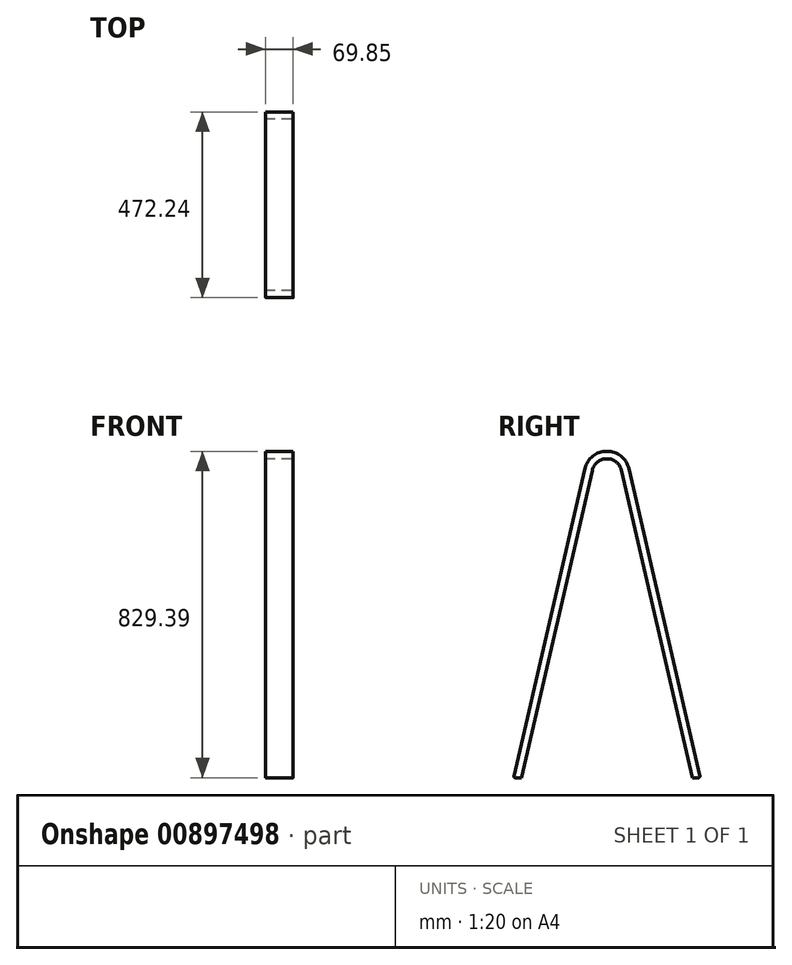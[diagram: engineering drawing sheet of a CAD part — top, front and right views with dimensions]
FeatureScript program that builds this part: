
annotation { "Feature Type Name" : "Feature", "Feature Type Description" : "" }
export const myFeature = defineFeature(function(context is Context, id is Id, definition is map)
    precondition{}
    {
        {
            var Q0;
            Q0=qCreatedBy(makeId("Right.planeOp"),FACE);
            var sketch = newSketch(context, id + "F0", { "sketchPlane" : qUnion([Q0])});
            skLineSegment(sketch, "E0", {"start": v(-210.57, 0) * mm, "end": v(-191.02, 0) * mm});
            skArc(sketch, "E1", {"start": v(63.5, 780.8) * mm, "mid": v(26.37, 810.34) * mm, "end": v(-10.75, 780.8) * mm});
            skLineSegment(sketch, "E2", {"start": v(63.5, 780.8) * mm, "end": v(243.76, 0) * mm});
            skLineSegment(sketch, "E3", {"start": v(-10.75, 780.8) * mm, "end": v(-191.02, 0) * mm});
            skLineSegment(sketch, "E4.0", {"start": v(-29.31, 785.1) * mm, "end": v(-210.57, 0) * mm});
            skLineSegment(sketch, "E4.2", {"start": v(82.06, 785.1) * mm, "end": v(263.3, 0) * mm});
            skArc(sketch, "E5.0", {"start": v(82.06, 785.1) * mm, "mid": v(26.37, 829.39) * mm, "end": v(-29.31, 785.1) * mm});
            skLineSegment(sketch, "E6.trimOffspring", {"start": v(243.76, 0) * mm, "end": v(263.3, 0) * mm});
            skPoint(sketch, "E7.start.orphan", {"position": v(26.37, 829.39) * mm});
            skSolve(sketch);
        }
        {
            var Q0;
            Q0=makeQuery(id+"F0.imprint","IMPRINT",FACE,{"disambiguationData":[TD([[makeQuery(id+"F0.imprint","IMPRINT",EDGE,{"derivedFrom":sQuery(id+"F0.wireOp",EDGE,"E0")}),1.0]])]});
            extrude(context, id + "F1", {"entities" : qUnion([Q0]), "depth" : 69.85 * mm, "offsetDistance" : 25.4 * mm});
        }
        {
            var Q0;
            Q0=makeQuery(id+"F1.opExtrude","SWEPT_EDGE",EDGE,{"disambiguationData":[OSD([sQuery(id+"F0.wireOp",EDGE,"E0"),sQuery(id+"F0.wireOp",EDGE,"E4.0")])]});
            var Q1;
            Q1=makeQuery(id+"F1.opExtrude","SWEPT_EDGE",EDGE,{"disambiguationData":[OSD([sQuery(id+"F0.wireOp",EDGE,"E4.2"),sQuery(id+"F0.wireOp",EDGE,"E6.trimOffspring")])]});
            fillet(context, id + "F2", {"entities" : qUnion([Q0, Q1]), "radius" : 3.17 * mm, "tangentPropagation" : true, "allowEdgeOverflow" : false});
        }
    });
